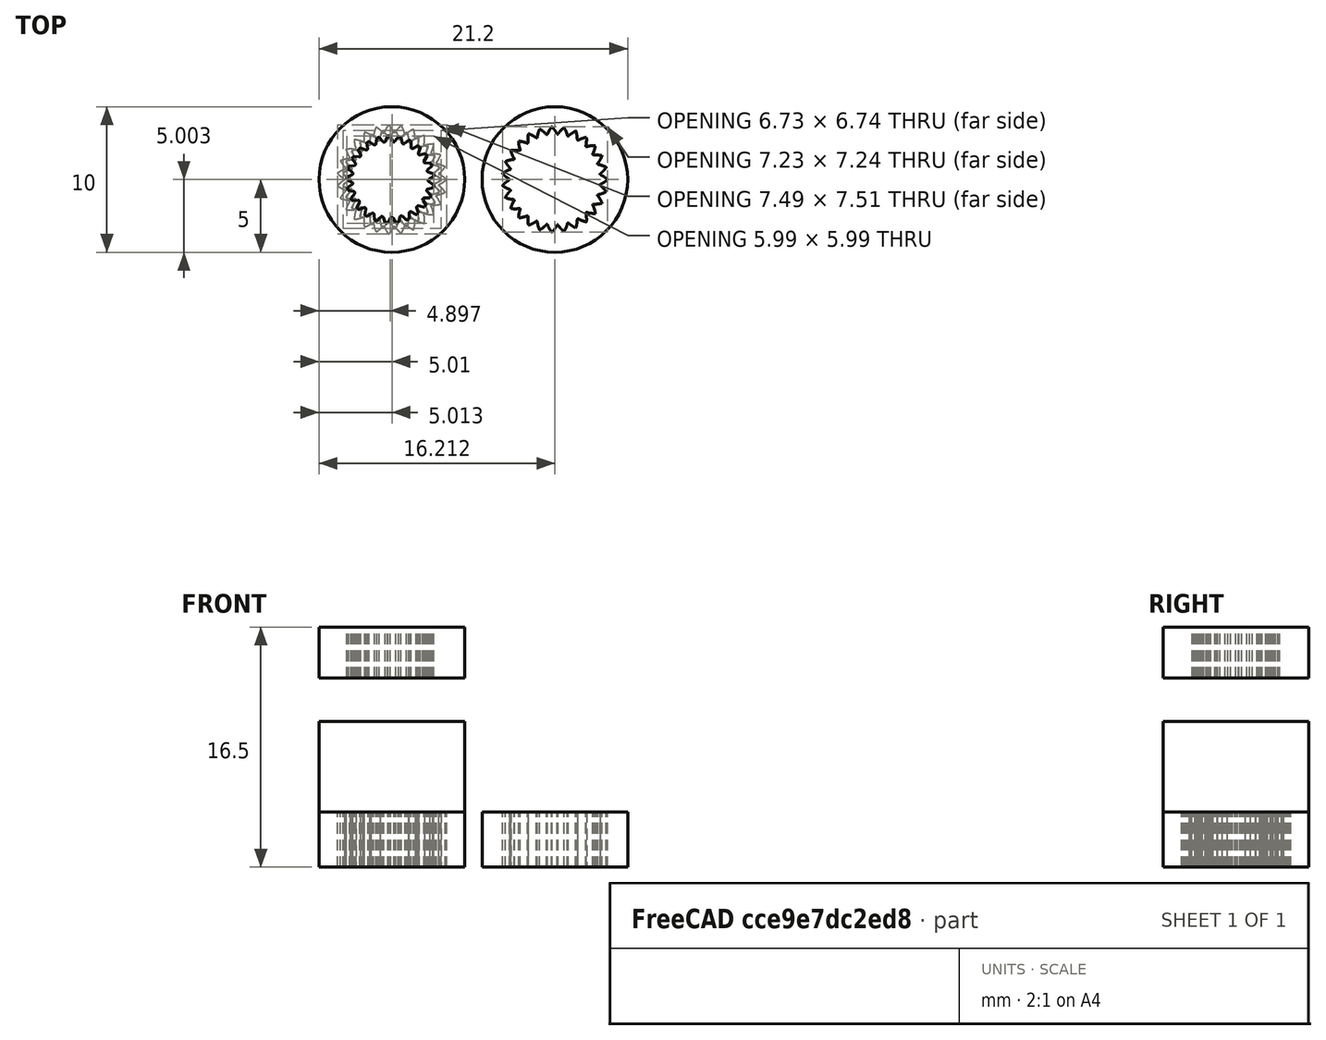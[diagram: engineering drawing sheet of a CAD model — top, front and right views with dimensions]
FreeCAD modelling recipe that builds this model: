
FCSTD DOCUMENT  (FreeCAD 0.18.4R)
Label: ext_gear
License: All rights reserved
LicenseURL: http://en.wikipedia.org/wiki/All_rights_reserved
objects: Part::FeaturePython×6, Part::Part2DObjectPython×5, Part::Extrusion×5, Part::Cylinder×5
note: 21 computed .brp shape members not serialized (recipe doc carries the construction recipe); baked Part::Feature solids carry a one-line shape summary decoded from their .brp

FEATURE [Part::Part2DObjectPython] InvoluteGear  # Draft 2D object (typed FeaturePython)
  ExternalGear = true
  HighPrecision = true
  Modules = 0.25
  NumberOfTeeth = 27
  PressureAngle = 36
  expr: Modules = 7 / 28
FEATURE [Part::FeaturePython] Cutout001  # WARN: FeaturePython — macro-defined, semantics opaque (R4)
  Placement = pos=(-10,-10.3,0) rot=(0,0,1;0rad)
  Tolerance = 0
FEATURE [Part::Extrusion] Extrude
  Base = -> InvoluteGear
  Dir = (0,0,1)
  DirMode = 2
  FaceMakerClass = Part::FaceMakerBullseye
  LengthFwd = 3.8
  LengthRev = 0
  Solid = true
  Symmetric = false
FEATURE [Part::Cylinder] Cylinder
  Angle = 360
  AttacherType = Attacher::AttachEngine3D
  Height = 3.8
  Radius = 5
FEATURE [Part::FeaturePython] Cutout  # WARN: FeaturePython — macro-defined, semantics opaque (R4)
  Base = -> Cylinder
  Placement = pos=(11.2,0,0) rot=(0,0,1;0rad)
  Tolerance = 0
  Tool = -> Extrude
FEATURE [Part::Part2DObjectPython] InvoluteGear001  # Draft 2D object (typed FeaturePython)
  ExternalGear = true
  HighPrecision = true
  Modules = 0.259259
  NumberOfTeeth = 27
  PressureAngle = 36
  expr: Modules = 7 / 27
FEATURE [Part::Extrusion] Extrude001
  Base = -> InvoluteGear001
  Dir = (0,0,1)
  DirMode = 2
  FaceMakerClass = Part::FaceMakerBullseye
  LengthFwd = 3.8
  LengthRev = 0
  Solid = true
  Symmetric = false
FEATURE [Part::Cylinder] Cylinder001
  Angle = 360
  AttacherType = Attacher::AttachEngine3D
  Height = 3.8
  Radius = 5
FEATURE [Part::FeaturePython] Cutout002  # WARN: FeaturePython — macro-defined, semantics opaque (R4)
  Base = -> Cylinder001
  Tolerance = 0
  Tool = -> Extrude001
FEATURE [Part::Part2DObjectPython] InvoluteGear002  # Draft 2D object (typed FeaturePython)
  ExternalGear = true
  HighPrecision = true
  Modules = 0.25
  NumberOfTeeth = 25
  PressureAngle = 36
  expr: Modules = 7 / 28
FEATURE [Part::Extrusion] Extrude002
  Base = -> InvoluteGear002
  Dir = (0,0,1)
  DirMode = 2
  FaceMakerClass = Part::FaceMakerBullseye
  LengthFwd = 3.8
  LengthRev = 0
  Solid = true
  Symmetric = false
FEATURE [Part::Cylinder] Cylinder002
  Angle = 360
  AttacherType = Attacher::AttachEngine3D
  Height = 3.8
  Radius = 5
FEATURE [Part::FeaturePython] Cutout003  # WARN: FeaturePython — macro-defined, semantics opaque (R4)
  Base = -> Cylinder002
  Tolerance = 0
  Tool = -> Extrude002
FEATURE [Part::Part2DObjectPython] InvoluteGear003  # Draft 2D object (typed FeaturePython)
  ExternalGear = true
  HighPrecision = true
  Modules = 0.25
  NumberOfTeeth = 25
  PressureAngle = 25
  expr: Modules = 7 / 28
FEATURE [Part::Extrusion] Extrude003
  Base = -> InvoluteGear003
  Dir = (0,0,1)
  DirMode = 2
  FaceMakerClass = Part::FaceMakerBullseye
  LengthFwd = 3.8
  LengthRev = 0
  Solid = true
  Symmetric = false
FEATURE [Part::Cylinder] Cylinder003
  Angle = 360
  AttacherType = Attacher::AttachEngine3D
  Height = 10
  Radius = 5
FEATURE [Part::FeaturePython] Cutout004  # WARN: FeaturePython — macro-defined, semantics opaque (R4)
  Base = -> Cylinder003
  Tolerance = 0
  Tool = -> Extrude003
FEATURE [Part::Part2DObjectPython] InvoluteGear004  # Draft 2D object (typed FeaturePython)
  ExternalGear = true
  HighPrecision = true
  Modules = 0.25
  NumberOfTeeth = 25
  PressureAngle = 30
  expr: Modules = 7 / 28
FEATURE [Part::Extrusion] Extrude004
  Base = -> InvoluteGear004
  Dir = (0,0,1)
  DirMode = 2
  FaceMakerClass = Part::FaceMakerBullseye
  LengthFwd = 3.8
  LengthRev = 0
  Solid = true
  Symmetric = false
FEATURE [Part::Cylinder] Cylinder004
  Angle = 360
  AttacherType = Attacher::AttachEngine3D
  Height = 3.8
  Radius = 5
FEATURE [Part::FeaturePython] Cutout005  # WARN: FeaturePython — macro-defined, semantics opaque (R4)
  Base = -> Cylinder004
  Tolerance = 0
  Tool = -> Extrude004
